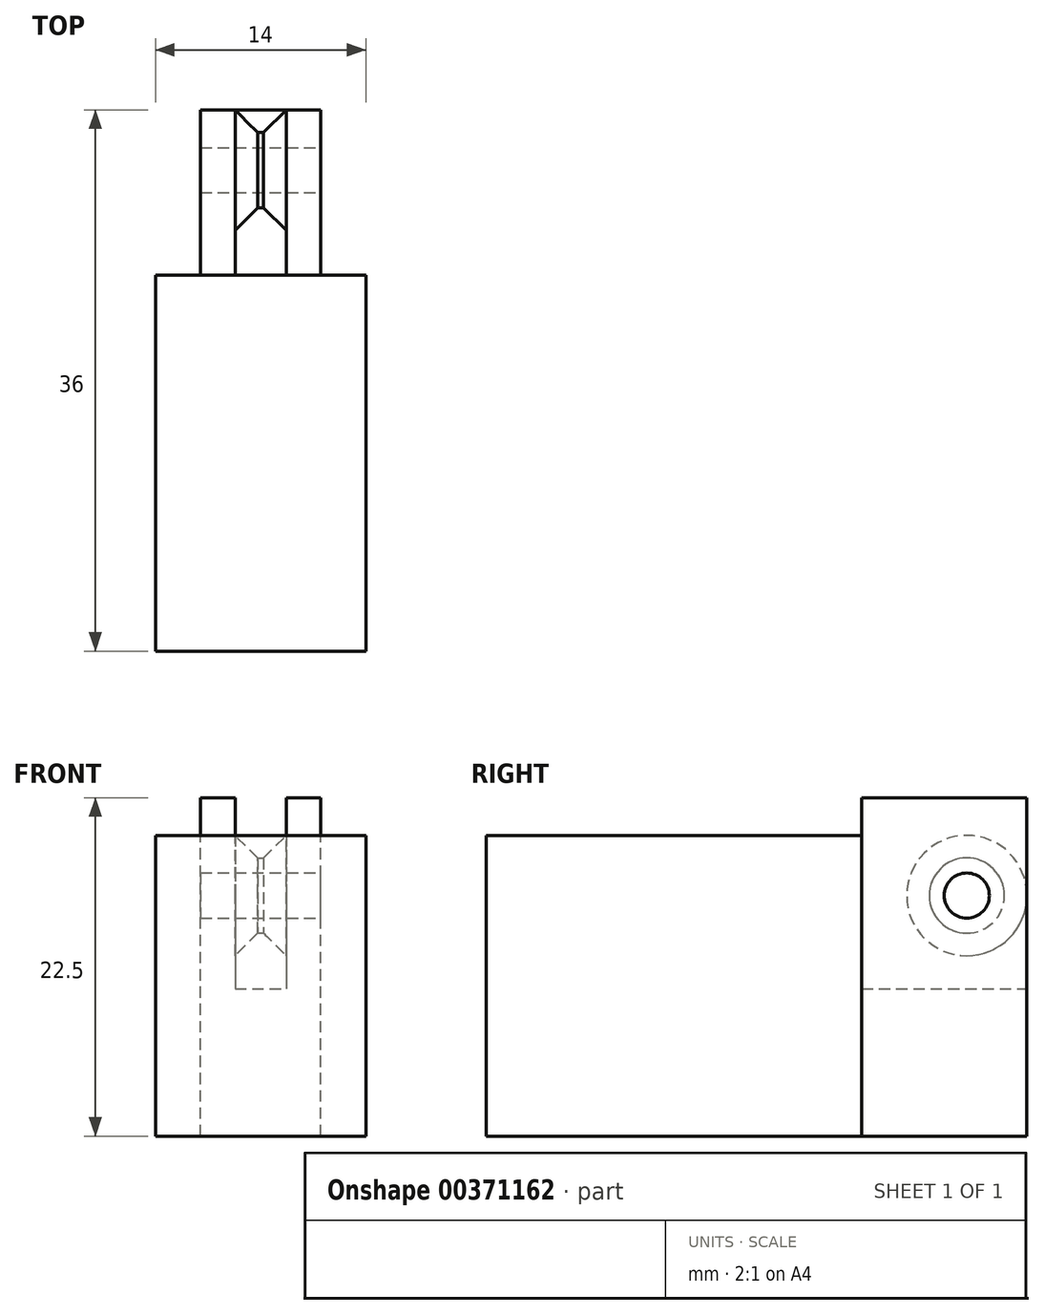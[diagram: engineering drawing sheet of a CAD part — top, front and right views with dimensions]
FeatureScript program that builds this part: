
annotation { "Feature Type Name" : "Feature", "Feature Type Description" : "" }
export const myFeature = defineFeature(function(context is Context, id is Id, definition is map)
    precondition{}
    {
        {
            var Q0;
            Q0=qCreatedBy(makeId("Front.planeOp"),FACE);
            var sketch = newSketch(context, id + "F0", { "sketchPlane" : qUnion([Q0])});
            skLineSegment(sketch, "E0", {"start": v(0, 0) * mm, "end": v(-4, 0) * mm});
            skLineSegment(sketch, "E1", {"start": v(-4, 0) * mm, "end": v(-4, 22.5) * mm});
            skLineSegment(sketch, "E2", {"start": v(-4, 22.5) * mm, "end": v(-1.7, 22.5) * mm});
            skLineSegment(sketch, "E3", {"start": v(-1.7, 22.5) * mm, "end": v(-1.7, 0) * mm, "construction": true});
            skPoint(sketch, "E3.endSnap0", {"position": v(-2, 0) * mm});
            skLineSegment(sketch, "E4", {"start": v(-1.7, 0) * mm, "end": v(-1.7, 9.8) * mm, "construction": true});
            skLineSegment(sketch, "E5", {"start": v(-1.7, 22.5) * mm, "end": v(-1.7, 9.8) * mm});
            skLineSegment(sketch, "E6", {"start": v(-1.7, 9.8) * mm, "end": v(0, 9.8) * mm});
            skLineSegment(sketch, "E7", {"start": v(0, 9.8) * mm, "end": v(0, 0) * mm});
            skSolve(sketch);
        }
        {
            var Q0;
            Q0=makeQuery(id+"F0.imprint","IMPRINT",FACE,{"disambiguationData":[TD([[makeQuery(id+"F0.imprint","IMPRINT",EDGE,{"derivedFrom":sQuery(id+"F0.wireOp",EDGE,"E0")}),-1.0]])]});
            extrude(context, id + "F1", {"entities" : qUnion([Q0]), "depth" : 11 * mm});
        }
        {
            var Q0;
            Q0=makeQuery(id+"F1.opExtrude","SWEPT_BODY",BODY,{"disambiguationData":[OSD([sQuery(id+"F0.wireOp",EDGE,"E0"),sQuery(id+"F0.wireOp",EDGE,"E1"),sQuery(id+"F0.wireOp",EDGE,"E2"),sQuery(id+"F0.wireOp",EDGE,"E5"),sQuery(id+"F0.wireOp",EDGE,"E6"),sQuery(id+"F0.wireOp",EDGE,"E7")])]});
            var Q1;
            Q1=makeQuery(id+"F1.opExtrude","SWEPT_FACE",FACE,{"disambiguationData":[OSD([sQuery(id+"F0.wireOp",EDGE,"E7")])]});
            mirror(context, id + "F2", {"operationType" : NewBodyOperationType.ADD, "entities" : qUnion([Q0]), "mirrorPlane" : qUnion([Q1])});
        }
        {
            var Q0;
            {var subQ0=makeQuery(id+"F1.opExtrude","CAP_FACE",FACE,{"disambiguationData":[OSD([sQuery(id+"F0.wireOp",EDGE,"E0"),sQuery(id+"F0.wireOp",EDGE,"E1"),sQuery(id+"F0.wireOp",EDGE,"E2"),sQuery(id+"F0.wireOp",EDGE,"E5"),sQuery(id+"F0.wireOp",EDGE,"E6"),sQuery(id+"F0.wireOp",EDGE,"E7")])],"isStart":false});Q0=makeQuery(id+"F2.boolean.opBoolean","MERGE",FACE,{"derivedFrom":[subQ0,makeQuery(id+"F2.opPattern","COPY",FACE,{"derivedFrom":subQ0,"instanceName":"1"})]});}
            var sketch = newSketch(context, id + "F3", { "sketchPlane" : qUnion([Q0])});
            skLineSegment(sketch, "E8", {"start": v(0, 0) * mm, "end": v(-7, 0) * mm, "construction": true});
            skLineSegment(sketch, "E9", {"start": v(0, 0) * mm, "end": v(-7, 0) * mm});
            skLineSegment(sketch, "E10", {"start": v(-7, 0) * mm, "end": v(-7, 20) * mm});
            skLineSegment(sketch, "E11", {"start": v(0, 0) * mm, "end": v(7, 0) * mm});
            skLineSegment(sketch, "E12", {"start": v(7, 0) * mm, "end": v(7, 20) * mm});
            skLineSegment(sketch, "E13", {"start": v(-7, 20) * mm, "end": v(7, 20) * mm});
            skSolve(sketch);
        }
        {
            var Q0;
            {var subQ3=sQuery(id+"F3.wireOp",EDGE,"E12");Q0=makeQuery(id+"F3.imprint","IMPRINT",FACE,{"disambiguationData":[TD([[makeQuery(id+"F3.imprint","IMPRINT",EDGE,{"derivedFrom":subQ3}),1.0]])]});}
            var Q1;
            {var subQ13=makeQuery(id+"F1.opExtrude","CAP_EDGE",EDGE,{"disambiguationData":[OSD([sQuery(id+"F0.wireOp",EDGE,"E6")])],"isStart":false});var subQ14=makeQuery(id+"F2.boolean.opBoolean","MERGE",EDGE,{"derivedFrom":[subQ13,makeQuery(id+"F2.opPattern","COPY",EDGE,{"derivedFrom":subQ13,"instanceName":"1"})]});Q1=makeQuery(id+"F3.imprint","IMPRINT",FACE,{"disambiguationData":[TD([[makeQuery(id+"F3.imprint","IMPRINT",EDGE,{"derivedFrom":subQ14}),-1.0]])]});}
            var Q2;
            {var subQ5=makeQuery(id+"F1.opExtrude","CAP_EDGE",EDGE,{"disambiguationData":[OSD([sQuery(id+"F0.wireOp",EDGE,"E6")])],"isStart":false});var subQ6=makeQuery(id+"F2.boolean.opBoolean","MERGE",EDGE,{"derivedFrom":[subQ5,makeQuery(id+"F2.opPattern","COPY",EDGE,{"derivedFrom":subQ5,"instanceName":"1"})]});Q2=makeQuery(id+"F3.imprint","IMPRINT",FACE,{"disambiguationData":[TD([[makeQuery(id+"F3.imprint","IMPRINT",EDGE,{"derivedFrom":subQ6}),1.0]])]});}
            var Q3;
            {var subQ3=sQuery(id+"F3.wireOp",EDGE,"E10");Q3=makeQuery(id+"F3.imprint","IMPRINT",FACE,{"disambiguationData":[TD([[makeQuery(id+"F3.imprint","IMPRINT",EDGE,{"derivedFrom":subQ3}),-1.0]])]});}
            extrude(context, id + "F4", {"entities" : qUnion([Q0, Q1, Q2, Q3]), "operationType" : NewBodyOperationType.ADD, "depth" : 25 * mm});
        }
        {
            var Q0;
            Q0=makeQuery(id+"F2.opPattern","COPY",FACE,{"derivedFrom":makeQuery(id+"F1.opExtrude","SWEPT_FACE",FACE,{"disambiguationData":[OSD([sQuery(id+"F0.wireOp",EDGE,"E1")])]}),"instanceName":"1"});
            var sketch = newSketch(context, id + "F5", { "sketchPlane" : qUnion([Q0])});
            skLineSegment(sketch, "E14", {"start": v(0, 16) * mm, "end": v(-4, 16) * mm, "construction": true});
            skLineSegment(sketch, "E15", {"start": v(-4, 16) * mm, "end": v(-4, 0) * mm, "construction": true});
            skCircle(sketch, "E16", {"center": v(-4, 16) * mm, "radius": 1.5 * mm});
            skCircle(sketch, "E17", {"center": v(-4, 16) * mm, "radius": 2.5 * mm});
            skSolve(sketch);
        }
        {
            var Q0;
            Q0=makeQuery(id+"F5.imprint","IMPRINT",FACE,{"disambiguationData":[TD([[makeQuery(id+"F5.imprint","IMPRINT",EDGE,{"derivedFrom":sQuery(id+"F5.wireOp",EDGE,"E16")}),1.0]])]});
            extrude(context, id + "F6", {"entities" : qUnion([Q0]), "operationType" : NewBodyOperationType.REMOVE, "oppositeDirection" : true, "depth" : 25 * mm});
        }
        {
            var Q0;
            Q0=makeQuery(id+"F5.imprint","IMPRINT",FACE,{"disambiguationData":[TD([[makeQuery(id+"F5.imprint","IMPRINT",EDGE,{"derivedFrom":sQuery(id+"F5.wireOp",EDGE,"E16")}),-1.0]])]});
            var Q1;
            Q1=makeQuery(id+"F1.opExtrude","SWEPT_FACE",FACE,{"disambiguationData":[OSD([sQuery(id+"F0.wireOp",EDGE,"E1")])]});
            extrude(context, id + "F7", {"entities" : qUnion([Q0]), "operationType" : NewBodyOperationType.ADD, "endBound" : BoundingType.UP_TO_SURFACE, "oppositeDirection" : true, "endBoundEntityFace" : qUnion([Q1]), "depth" : 25 * mm});
        }
        {
            var Q0;
            Q0=makeQuery(id+"F7.boolean.opBoolean","INTERSECT",EDGE,{"derivedFrom":[makeQuery(id+"F1.opExtrude","SWEPT_FACE",FACE,{"disambiguationData":[OSD([sQuery(id+"F0.wireOp",EDGE,"E5")])]}),makeQuery(id+"F7.opExtrude","SWEPT_FACE",FACE,{"disambiguationData":[OSD([sQuery(id+"F5.wireOp",EDGE,"E17")])]})]});
            chamfer(context, id + "F8", {"entities" : qUnion([Q0]), "width" : 1.5 * mm, "tangentPropagation" : true});
        }
        {
            var Q0;
            Q0=makeQuery(id+"F7.boolean.opBoolean","INTERSECT",EDGE,{"derivedFrom":[makeQuery(id+"F2.opPattern","COPY",FACE,{"derivedFrom":makeQuery(id+"F1.opExtrude","SWEPT_FACE",FACE,{"disambiguationData":[OSD([sQuery(id+"F0.wireOp",EDGE,"E5")])]}),"instanceName":"1"}),makeQuery(id+"F7.opExtrude","SWEPT_FACE",FACE,{"disambiguationData":[OSD([sQuery(id+"F5.wireOp",EDGE,"E17")])]})]});
            chamfer(context, id + "F9", {"entities" : qUnion([Q0]), "width" : 1.5 * mm, "tangentPropagation" : true});
        }
        {
            var Q0;
            Q0=qCreatedBy(makeId("Front.planeOp"),FACE);
            var sketch = newSketch(context, id + "F10", { "sketchPlane" : qUnion([Q0])});
            skCircle(sketch, "E18", {"center": v(0, 16.35) * mm, "radius": 7.16 * mm});
            skSolve(sketch);
        }
    });
